# Revit family: PRD_AR_Snks_MaximaCommercialSink_MAXL227-260
name_source: partatom
category: Plumbing Fixtures
revit_build: Autodesk Revit 2018 (Build: 20190510_1515(x64)
units: mm (PartAtom-declared; Revit-internal decimal feet)

## family parameters
Always vertical = Yes
Cut with Voids When Loaded = No
OmniClass Number = 23.45.05.14.14
OmniClass Title = Sinks/Lavatories
Part Type = Normal
Room Calculation Point = No
Round Connector Dimension = Use Diameter
Shared = No
Work Plane-Based = No

## types (1)
- MAXL227-260
    Accessories = Shelf
    Arrangement = Double bowl sink with relief pattern left hand drainer
    AssetType = Fixed
    BIMObjectName = PRD_AR_KitchenSinks_MaximaCommercialSink_MAXL227-260
    BracketsMaterial = PRD_AR_StainlessSteel_SatinFinished
    Category = Pr_40_20_96_45, Kitchen sinks
    Color = stainless steel
    Constituents = Underframe MAXF260-70
    ConstructionFrameAssembly = Underframe to screw with Franke commercial sink
    ConstructionFrameFinish = satin finished
    ConstructionFrameMaterial = Square tubular leg frame, stainless steel 1.4301
    Description = Commercial sink and underframe welded together, stainless steel, surface satin finished, material thickness 1 mm, two deep drawn seamless welded bowls, without overflow and 80 mm tap ledge, 1 1/2" waste with two part overflow tube consisting of perforated stainless steel tube and plastic tube, drain board with riffle and slanted to bowl, storage board left or right, drain board on opposite side of drain board, drain board with reinforced stainless steel bracket, 100 mm rear upstand, underframe with 300 mm cover, feet 40 x 40 mm and height adjustable to 25 mm, cross stud on backside for better stability, drilling holes for wall mounting prelasered.
Drain board left
    DrainSize = DN 40 (1 1/2 inch.)
    DurationUnit = year
    Features = stainless steel, 1.00 mm, satin finished
    Finish = satin finished
    GrossWeight = 37.00 kg
    IfcExportAs = IfcSanitaryTerminalType
    IfcExportType = SINK
    Manufacturer = KWC Group AG
    ManufacturerName = KWC Group AG
    ManufacturerURL = www.kwc.com
    Material = stainless steel
    MaterialCode = stainless steel 1.4301
    Model = MAXL227-260
    ModelNumber = 2000057613
    ModelReference = MAXL227-260
    NBSDescription = Commercial stainless steel sinks
    NBSReference = 45-35-15/432
    Name = Maxima catering sink MAXL227-260
    NetWeight = 34.00 kg
    NominalDepth = 700 mm  [stored 2.29659 ft]
    NominalHeight = 432 mm  [stored 1.41732 ft]
    NominalWidth = 2600 mm  [stored 8.53018 ft]
    OverallDimensionsDepthMaximum = 700 mm  [stored 2.29659 ft]
    OverallDimensionsHeightMaximum = 1000 mm  [stored 3.28084 ft]
    OverallDimensionsLengthMaximum = 2600 mm  [stored 8.53018 ft]
    ProductInformation = https://pim.kwc.com
    Shape = Rectangular
    SinkMaterial = PRD_AR_StainlessSteel_SatinFinished
    SinkMounting = Other
    SinkType = Rinsing
    Size = 2600 x 432 x 700 mm
    URL = www.kwc.com
    UnderframeMaterial = PRD_AR_StainlessSteel_SatinFinished
    Uniclass2015Code = Pr_40_20_96_45
    Uniclass2015Title = Kitchen sinks
    Uniclass2015Version = Products v1.10
    Version = 1
    WarrantyDurationUnit = year
    WashBowlsDepthMaximum = 300 mm
    WashBowlsLengthMaximum = 600 mm  [stored 1.9685 ft]
    WashBowlsTapArrangement = 80 mm tap ledge
    WashBowlsWasteArrangement = Right-Back-Corner / Left-Back-Corner
    WashBowlsWasteDiameter = DN 40 (1 1/2 inch.)
    WashBowlsWasteMaterial = stainless steel
    WashBowlsWidthMaximum = 500 mm  [stored 1.64042 ft]
    WasteSize = 40  [stored 0.131234 ft]

note: [stored X ft] marks values corroborated as IEEE doubles in the binary element streams (Revit-internal decimal feet)

## geometry (parser evidence)
native form markers: Sweep x11
no freeform markers — native parametric forms only
